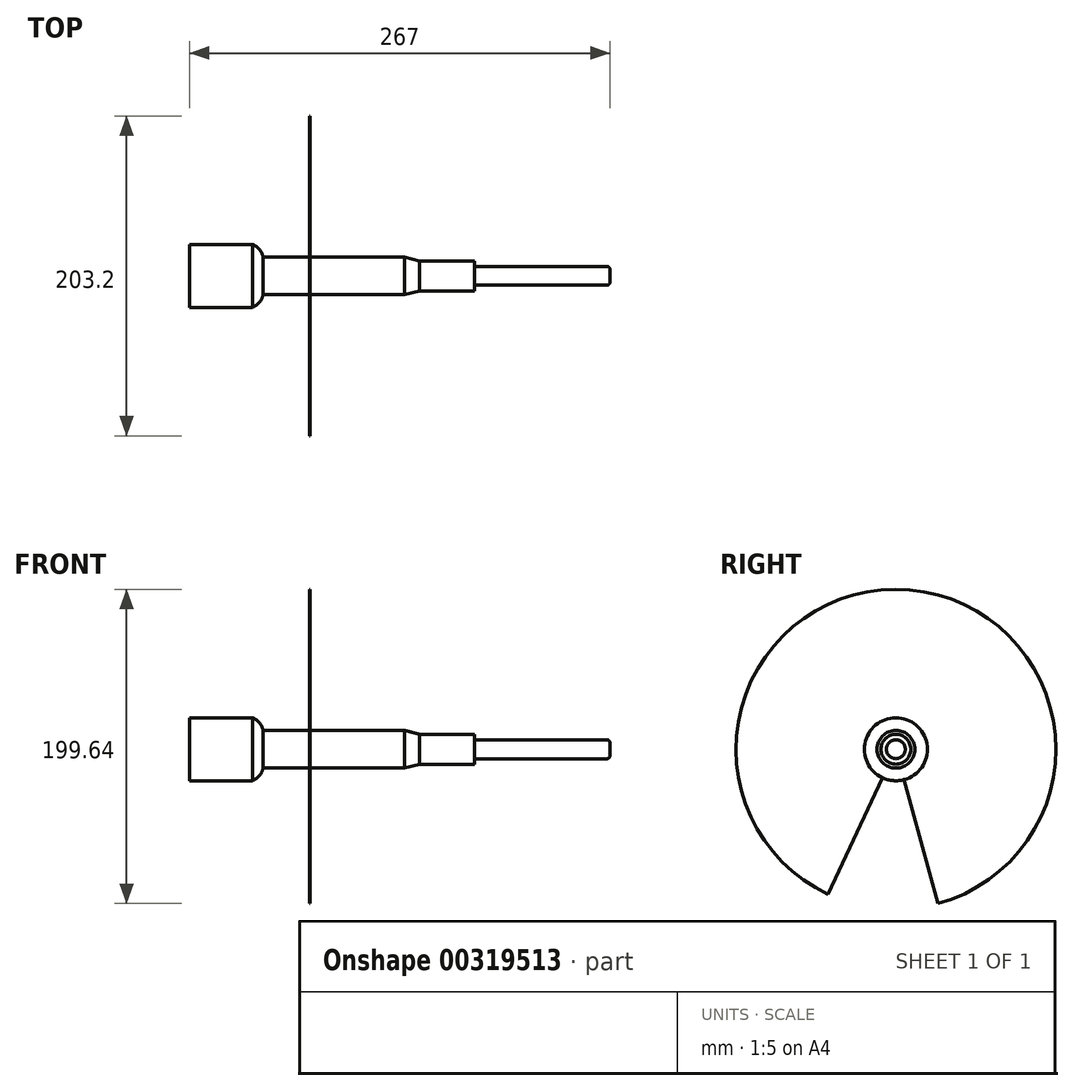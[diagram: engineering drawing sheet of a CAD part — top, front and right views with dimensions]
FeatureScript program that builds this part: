
annotation { "Feature Type Name" : "Feature", "Feature Type Description" : "" }
export const myFeature = defineFeature(function(context is Context, id is Id, definition is map)
    precondition{}
    {
        {
            var Q0;
            Q0=qCreatedBy(makeId("Front.planeOp"),FACE);
            var sketch = newSketch(context, id + "F0", { "sketchPlane" : qUnion([Q0])});
            skLineSegment(sketch, "E0", {"start": v(0, 0) * mm, "end": v(267, 0) * mm, "construction": true});
            skLineSegment(sketch, "E1", {"start": v(267, 0) * mm, "end": v(267, 6) * mm});
            skLineSegment(sketch, "E2", {"start": v(267, 6) * mm, "end": v(181, 6) * mm});
            skLineSegment(sketch, "E3", {"start": v(181, 6) * mm, "end": v(181, 9.5) * mm});
            skLineSegment(sketch, "E4", {"start": v(181, 9.5) * mm, "end": v(146, 9.5) * mm});
            skLineSegment(sketch, "E5", {"start": v(0, 0) * mm, "end": v(0, 20) * mm});
            skLineSegment(sketch, "E6", {"start": v(0, 20) * mm, "end": v(40, 20) * mm});
            skLineSegment(sketch, "E7", {"start": v(146, 9.5) * mm, "end": v(136.67, 12) * mm});
            skLineSegment(sketch, "E8", {"start": v(136.67, 12) * mm, "end": v(46.67, 12) * mm});
            skArc(sketch, "E9", {"start": v(46.67, 12) * mm, "mid": v(44.34, 16.84) * mm, "end": v(40, 20) * mm});
            skLineSegment(sketch, "E10", {"start": v(0, 0) * mm, "end": v(267, 0) * mm});
            skSolve(sketch);
        }
        {
            var Q0;
            Q0=makeQuery(id+"F0.imprint","IMPRINT",FACE,{"disambiguationData":[TD([[makeQuery(id+"F0.imprint","IMPRINT",EDGE,{"derivedFrom":sQuery(id+"F0.wireOp",EDGE,"E1")}),1.0]])]});
            var Q1;
            Q1=sQuery(id+"F0.wireOp",EDGE,"E10");
            revolve(context, id + "F1", {"entities" : qUnion([Q0]), "axis" : qUnion([Q1]), "revolveType" : RevolveType.FULL});
        }
        {
            var Q0;
            Q0=makeQuery(id+"F1.opRevolve","SWEPT_EDGE",EDGE,{"disambiguationData":[OSD([sQuery(id+"F0.wireOp",EDGE,"E1"),sQuery(id+"F0.wireOp",EDGE,"E2")])]});
            fillet(context, id + "F2", {"entities" : qUnion([Q0]), "radius" : 2 * mm, "tangentPropagation" : true, "allowEdgeOverflow" : false});
        }
        {
            var Q0;
            Q0=qCreatedBy(makeId("Right.planeOp"),FACE);
            cPlane(context, id + "F3", {"entities" : qUnion([Q0]), "cplaneType" : CPlaneType.OFFSET, "offset" : 76.2 * mm, "width" : 150 * mm, "height" : 150 * mm});
        }
        {
            var Q0;
            Q0=qCreatedBy(id+"F3.planeOp",FACE);
            var sketch = newSketch(context, id + "F4", { "sketchPlane" : qUnion([Q0])});
            skLineSegment(sketch, "E11", {"start": v(0, 0) * mm, "end": v(5.25, -19.3) * mm});
            skLineSegment(sketch, "E12", {"start": v(0, 0) * mm, "end": v(-8.48, -18.11) * mm});
            skLineSegment(sketch, "E13", {"start": v(5.25, -19.3) * mm, "end": v(26.67, -98.04) * mm});
            skLineSegment(sketch, "E14", {"start": v(-5.09, -10.87) * mm, "end": v(-5.09, -10.87) * mm});
            skLineSegment(sketch, "E15", {"start": v(-8.48, -18.11) * mm, "end": v(-43.07, -92.02) * mm});
            skLineSegment(sketch, "E16", {"start": v(26.67, -98.04) * mm, "end": v(-43.07, -92.02) * mm, "construction": true});
            skArc(sketch, "E17", {"start": v(26.67, -98.04) * mm, "mid": v(8.73, 101.22) * mm, "end": v(-43.07, -92.02) * mm});
            skArc(sketch, "E18", {"start": v(-43.07, -92.02) * mm, "mid": v(-8.73, -101.22) * mm, "end": v(26.67, -98.04) * mm, "construction": true});
            skLineSegment(sketch, "E19", {"start": v(0, 0) * mm, "end": v(20, 0) * mm});
            skLineSegment(sketch, "E20", {"start": v(0, 0) * mm, "end": v(0, 20) * mm});
            skLineSegment(sketch, "E21", {"start": v(0, 0) * mm, "end": v(-20, 0) * mm});
            skLineSegment(sketch, "E22", {"start": v(0, 0) * mm, "end": v(15, 13.22) * mm});
            skLineSegment(sketch, "E23", {"start": v(0, 0) * mm, "end": v(-14.97, 13.26) * mm});
            skCircle(sketch, "E24", {"center": v(0, 0) * mm, "radius": 20 * mm});
            skSolve(sketch);
        }
        {
            var Q0;
            Q0=makeQuery(id+"F4.imprint","IMPRINT",FACE,{"disambiguationData":[TD([[makeQuery(id+"F4.imprint","IMPRINT",EDGE,{"derivedFrom":sQuery(id+"F4.wireOp",EDGE,"E13")}),1.0]])]});
            extrude(context, id + "F5", {"entities" : qUnion([Q0]), "depth" : 0.25 * mm});
        }
    });
